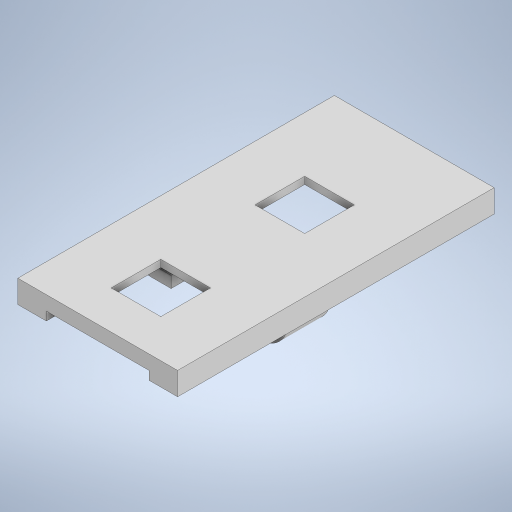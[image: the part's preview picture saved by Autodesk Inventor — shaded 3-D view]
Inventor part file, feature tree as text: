
AUTODESK INVENTOR PART (.ipt)
format: ipt  version: 2023 (Build 270158000, 158)  size: 648,704 bytes
history: native  units: in
note: dims shown in document units (in); Inventor stores cm internally (conversion verified against a paired STEP export)
features: extrude x17, sketch x15, fillet x2
ambient origin geometry x8: Origin, YZ Plane, XZ Plane, XY Plane, X Axis, Y Axis, Z Axis, Center Point
bodies: Solid1 (feature_tree)
feature tree (34):
  extrude  "Extrusion1"  Depth=4.5in
  extrude  "Extrusion2"  Depth=0.2in
  fillet  "Fillet1"  Radius=1.4in
  extrude  "Extrusion3"  Depth=0.125in
  extrude  "Extrusion4"  Depth=2.2875in
  extrude  "Extrusion5"  Depth=0.5437in
  sketch  "Sketch6"  dims[d13=0.75in d14=1.4in d15=0.0in]
  extrude  "Extrusion6"  Depth=1.4in TaperAngle=0.0deg
  extrude  "Extrusion9"  Depth=0.1in
  extrude  "Extrusion10"  Depth=0.1in
  extrude  "Extrusion11"  Depth=0.25in
  extrude  "Extrusion12"  Depth=0.15in
  extrude  "Extrusion13"  Depth=0.7in
  extrude  "Extrusion14"  Depth=0.1in
  extrude  "Extrusion15"  Depth=0.615in
  extrude  "Extrusion16"  Depth=1.1in
  fillet  "Fillet2"  Radius=0.21in
  extrude  "Extrusion18"  Depth=0.5in
  extrude  "Extrusion19"  Depth=0.5in
  extrude  "Extrusion20"  Depth=0.5in
  sketch  "Sketch1"  dims[d0=7.0in d1=4.5in]
  sketch  "Sketch2"  dims[d2=1.5in d3=0.0in d4=0.2in d5=1.4in d6=0.0in]
  sketch  "Sketch3"  dims[d7=0.125in d8=0.25in]
  sketch  "Sketch4"  dims[d9=0.25in d10=2.2875in]
  sketch  "Sketch5"  dims[d11=3.4125in d12=0.5437in]
  sketch  "Sketch8"  dims[d16=0.1in d17=0.14in]
  sketch  "Sketch9"  dims[d18=0.1in d19=0.275in]
  sketch  "Sketch10"  dims[d20=0.35in d21=0.25in]
  sketch  "Sketch11"  dims[d22=0.15in d23=0.15in]
  sketch  "Sketch12"  dims[d24=0.25in d25=0.7in]
  sketch  "Sketch13"  dims[d26=0.1in d27=0.1in]
  sketch  "Sketch15"  dims[d28=0.25in d29=0.615in]
  sketch  "Sketch16"  dims[d30=0.25in d31=1.1in d32=0.21in]
  sketch  "Sketch17"  dims[d33=0.3075in d34=0.5575in d35=1.65in d36=0.3075in d37=0.21in d38=0.5575in d39=2.1in d40=0.1in d41=0.1in d42=0.3in d43=0.1in d44=0.25in d45=0.615in d46=2.4in d47=0.11in d48=2.51in d49=0.5575in d50=0.1in d51=0.615in d52=0.175in d53=0.175in d54=0.1in d55=0.1in d56=0.25in d57=3.15in d58=0.1in d59=0.515in d60=0.05in d61=0.0in d62=0.1562in d63=0.1562in d64=0.2175in d65=0.2175in d66=0.2175in d67=0.2175in d68=0.2175in d69=0.2175in d70=0.63in d71=0.63in d72=0.63in d73=0.63in d74=0.8812in d76=2.25in d77=0.3in d78=0.3in d79=0.3in d80=0.3in d81=0.3in d82=0.625in d83=0.625in d84=0.625in d85=0.625in d86=1.0in d87=3.1in d88=3.1in d89=3.1in d90=3.1in d91=3.1in d92=1.0in d93=0.0in d97=0.4in d98=0.4in d99=0.4in d100=0.4in d101=0.4in d102=0.05in d103=0.0in d124=0.0688in d125=0.0in d126=0.25in d127=0.275in d128=0.25in d129=0.25in d130=0.25in d131=2.1in d132=0.125in d133=0.0625in d134=0.05in d135=0.0in d142=0.0375in d143=0.0in d144=2.0in d145=0.78in d146=0.0725in d147=0.3in d148=0.14in d149=0.1in d150=0.7in d151=0.2in d152=0.0in d153=0.075in d154=0.125in d155=0.0in d156=0.28in d157=2.5in d158=0.49in d159=0.25in d160=0.0in d161=0.45in d162=0.081in d163=0.0in d164=0.45in d177=0.075in d178=0.0in d179=0.125in d187=2.8in d189=0.04in d190=0.04in d191=0.04in d192=0.04in d193=0.04in d194=0.45in d195=0.0765in d196=0.076in d197=3.325in d198=0.254in d199=0.2535in d202=0.075in d203=0.125in d204=0.075in d205=0.125in d206=0.1875in d207=0.1875in d208=0.1875in d209=0.65in d210=0.65in d211=0.65in d212=0.125in d213=0.075in d214=0.025in d215=2.0in d216=0.5in d217=0.0in d218=0.0in d219=0.28in d220=0.14in d221=0.245in d222=0.28in d223=7.0in d224=0.0in d225=7.0in d226=0.0in]
